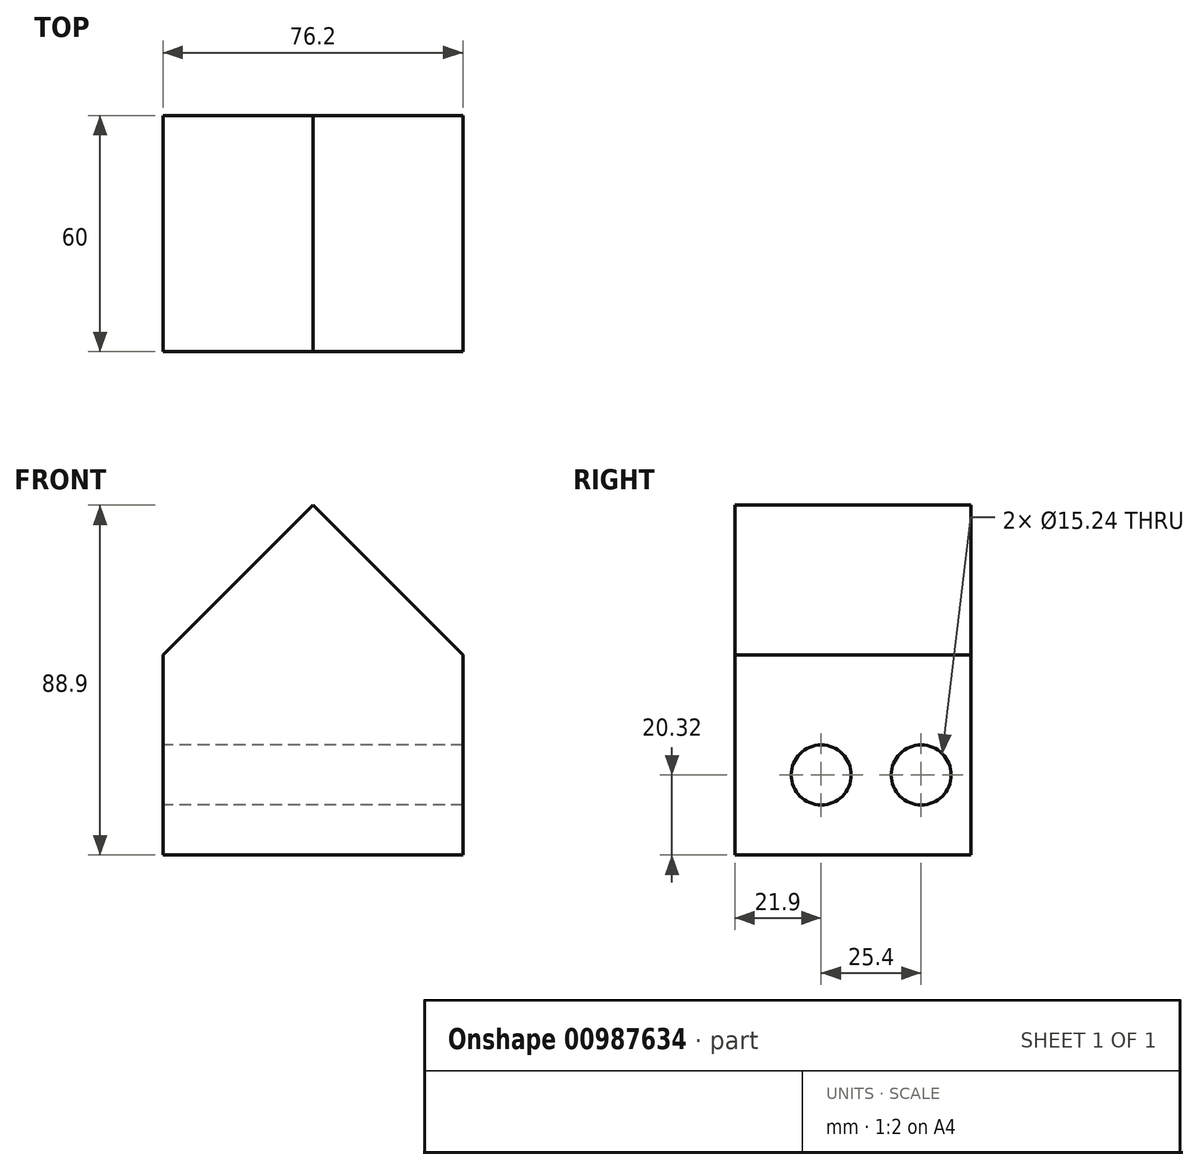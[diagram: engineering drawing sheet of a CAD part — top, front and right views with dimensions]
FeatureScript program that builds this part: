
annotation { "Feature Type Name" : "Feature", "Feature Type Description" : "" }
export const myFeature = defineFeature(function(context is Context, id is Id, definition is map)
    precondition{}
    {
        {
            var Q0;
            Q0=qCreatedBy(makeId("Front.planeOp"),FACE);
            var sketch = newSketch(context, id + "F0", { "sketchPlane" : qUnion([Q0])});
            skLineSegment(sketch, "E0.bottom", {"start": v(0, 0) * mm, "end": v(76.2, 0) * mm});
            skLineSegment(sketch, "E0.top", {"start": v(0, 50.8) * mm, "end": v(76.2, 50.8) * mm});
            skLineSegment(sketch, "E0.left", {"start": v(0, 0) * mm, "end": v(0, 50.8) * mm});
            skLineSegment(sketch, "E0.right", {"start": v(76.2, 0) * mm, "end": v(76.2, 50.8) * mm});
            skLineSegment(sketch, "E1", {"start": v(0, 50.8) * mm, "end": v(38.1, 88.9) * mm});
            skLineSegment(sketch, "E2", {"start": v(38.1, 88.9) * mm, "end": v(76.2, 50.8) * mm});
            skSolve(sketch);
        }
        {
            var Q0;
            Q0 = qSketchRegion(id + "F0", true);
            extrude(context, id + "F1", {"entities" : qUnion([Q0]), "depth" : 60 * mm, "offsetDistance" : 25.4 * mm});
        }
        {
            var Q0;
            Q0=makeQuery(id+"F1.opExtrude","SWEPT_FACE",FACE,{"disambiguationData":[OSD([sQuery(id+"F0.wireOp",EDGE,"E0.left")])]});
            var sketch = newSketch(context, id + "F2", { "sketchPlane" : qUnion([Q0])});
            skCircle(sketch, "E3", {"center": v(12.7, 20.32) * mm, "radius": 7.62 * mm});
            skCircle(sketch, "E4", {"center": v(38.1, 20.32) * mm, "radius": 7.62 * mm});
            skSolve(sketch);
        }
        {
            var Q0;
            Q0=makeQuery(id+"F2.imprint","IMPRINT",FACE,{"disambiguationData":[TD([[makeQuery(id+"F2.imprint","IMPRINT",EDGE,{"derivedFrom":sQuery(id+"F2.wireOp",EDGE,"E3")}),1.0]])]});
            extrude(context, id + "F3", {"entities" : qUnion([Q0]), "operationType" : NewBodyOperationType.REMOVE, "endBound" : BoundingType.THROUGH_ALL, "oppositeDirection" : true, "depth" : 254 * mm, "offsetDistance" : 25.4 * mm});
        }
        {
            var Q0;
            Q0 = qSketchRegion(id + "F2", true);
            extrude(context, id + "F4", {"entities" : qUnion([Q0]), "operationType" : NewBodyOperationType.REMOVE, "endBound" : BoundingType.THROUGH_ALL, "oppositeDirection" : true, "depth" : 127 * mm, "offsetDistance" : 25.4 * mm});
        }
    });
